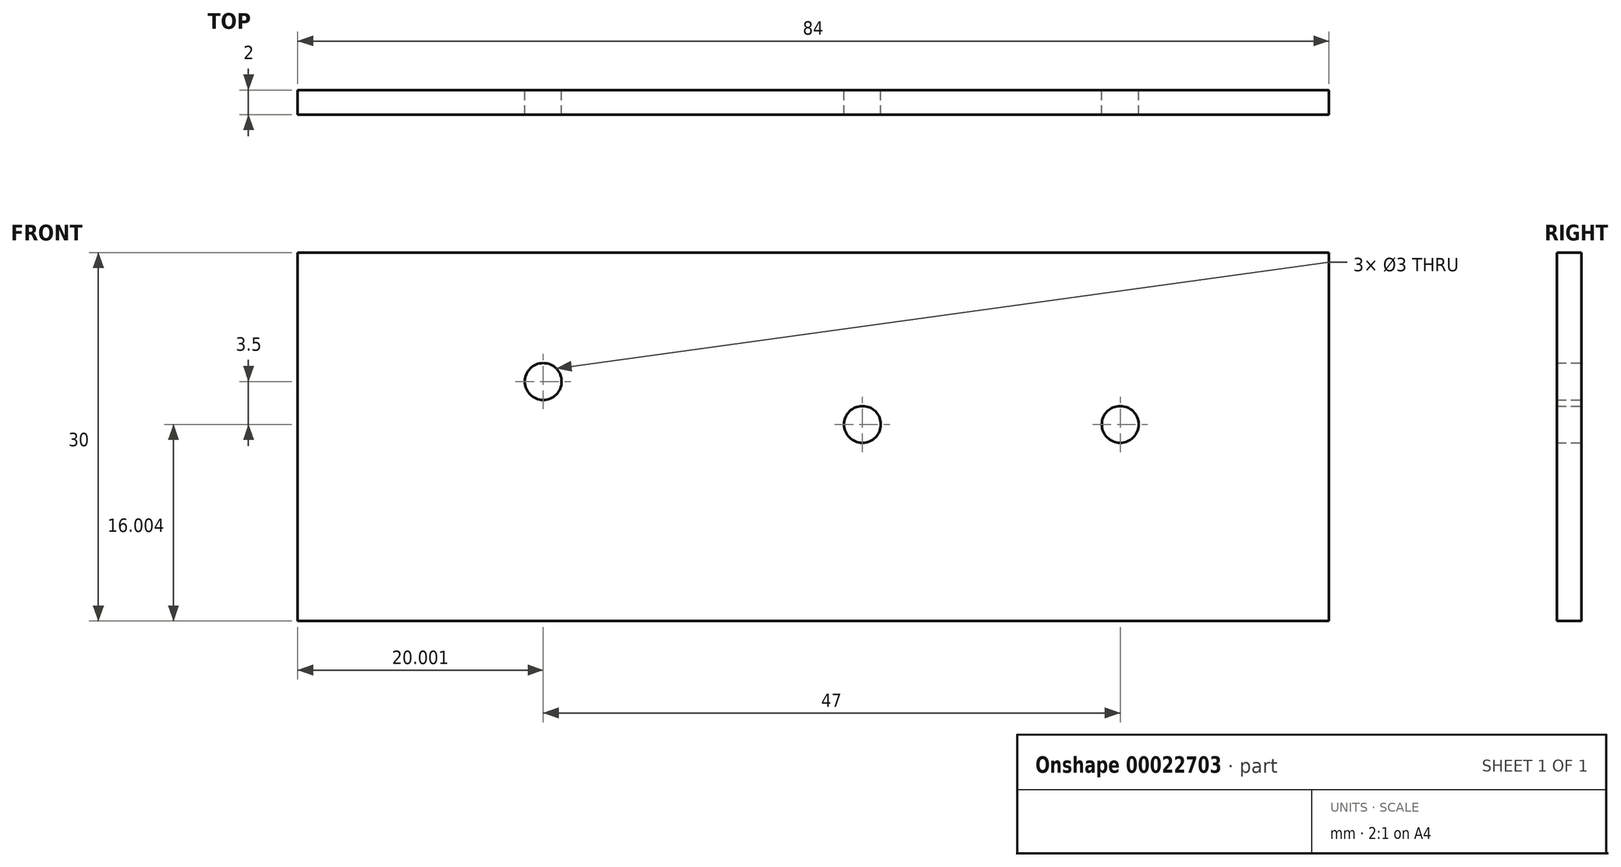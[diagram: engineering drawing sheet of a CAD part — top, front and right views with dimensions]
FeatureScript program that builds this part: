
annotation { "Feature Type Name" : "Feature", "Feature Type Description" : "" }
export const myFeature = defineFeature(function(context is Context, id is Id, definition is map)
    precondition{}
    {
        {
            var Q0;
            Q0=qCreatedBy(makeId("Front.planeOp"),FACE);
            var sketch = newSketch(context, id + "F0", { "sketchPlane" : qUnion([Q0])});
            skLineSegment(sketch, "E0.top", {"start": v(-140.28, 17) * mm, "end": v(-56.28, 17) * mm});
            skLineSegment(sketch, "E1", {"start": v(-120.28, 47) * mm, "end": v(-100.28, 47) * mm});
            skCircle(sketch, "E2", {"center": v(-120.28, 36.5) * mm, "radius": 1.5 * mm});
            skCircle(sketch, "E3", {"center": v(-73.28, 33) * mm, "radius": 1.5 * mm});
            skLineSegment(sketch, "E4", {"start": v(-88.28, 47) * mm, "end": v(-73.28, 47) * mm});
            skCircle(sketch, "E5", {"center": v(-94.28, 33) * mm, "radius": 1.5 * mm});
            skLineSegment(sketch, "E6", {"start": v(-100.28, 17) * mm, "end": v(-88.28, 17) * mm});
            skLineSegment(sketch, "E7", {"start": v(-73.28, 47) * mm, "end": v(-58.28, 47) * mm});
            skLineSegment(sketch, "E0.bottom", {"start": v(-140.28, 47) * mm, "end": v(-56.28, 47) * mm});
            skLineSegment(sketch, "E0.left", {"start": v(-140.28, 47) * mm, "end": v(-140.28, 17) * mm});
            skLineSegment(sketch, "E0.right", {"start": v(-56.28, 47) * mm, "end": v(-56.28, 17) * mm});
            skLineSegment(sketch, "E8", {"start": v(-140.28, 47) * mm, "end": v(-120.28, 47) * mm});
            skSolve(sketch);
        }
        {
            var Q0;
            Q0=makeQuery(id+"F0.imprint","IMPRINT",FACE,{"disambiguationData":[TD([[makeQuery(id+"F0.imprint","IMPRINT",EDGE,{"derivedFrom":sQuery(id+"F0.wireOp",EDGE,"E2")}),-1.0]])]});
            extrude(context, id + "F1", {"entities" : qUnion([Q0]), "depth" : 2 * mm});
        }
    });
